# Revit family: Roof-Windows_VELUX_GGLS(2)
name_source: partatom
category: Windows
revit_build: Autodesk Revit 2015 (Build: 20140606_1530(x64)
units: mm (PartAtom-declared; Revit-internal decimal feet)

## types (1)
- GGL Studio - 3x FK06
    AllowedRoofSlope = 15°-90°
    Analytic Construction = <None>
    Angle = 0.00°
    Assembly Code = B3020110
    AssemblyPlace = insitu
    CladdingMaterial = Two layers of aluminium
    CoatingInterior = white paint color NCS 0500-N
    Description = https://bimobject.com
    DistanceBetweenPanels = 588.5 mm  [stored 1.93077 ft]
    Edition number = 1
    FireExit = No
    FireRating = 0
    FlashingMaterial = Two layers of aluminium
    FrameArea = 0.75 m²
    Function = 2 x pivot hung roof window + 1 fixed
    GlassColour = Clear
    GlassLayers = 0
    GlassThickness1 = 0 mm  [stored 0 ft]
    GlassThickness2 = 0 mm  [stored 0 ft]
    GlassThickness3 = 0 mm  [stored 0 ft]
    Glazing = Glass
    GlazingArea = 1.41 m²
    GlazingAreaFraction = 0
    HasDrive = No
    HasExteriorShading = No
    HasInteriorShading = No
    HasSillExternal = Yes
    HasSillInternal = Yes
    Height = 1178 mm  [stored 3.86483 ft]
    Infiltration = 0
    IsExternal = Yes
    IsLaminated = Yes
    IsSolarPowered = No
    IsTempered = Yes
    IsWired = No
    LiningBendFromFrame = 66 mm
    LiningBendFromRoof = 155.3 mm  [stored 0.509514 ft]
    Manufacturer = VELUX A/S
    MaterialExterior = Aluminium. Color NCS 7500-N
    Model = GGLS
    OffsetFromRoof = 135.5 mm
    OpenWindow = No
    OpeningLines = Yes
    Operation = MANUAL
    PanelOffset = -119 mm
    PanelWidth = 641.8 mm
    PerimeterGlazing = 8.79 mm
    PerimeterWindow = 6.03 mm
    Product Guid = 619879da-f779-4aaa-8708-ee59bcbfb10d
    Product data url = https://www.bimobject.com
    ShadingCoefficient = 0
    SolarAbsorption = 0
    SolarHeatGainTransmittance = 0
    SolarReflectance = 0
    SolarTransmittance = 0
    ThermalBridgeGlazing = 0
    ThermalBridgeInstallation = 0
    ThermalTransmittance = 0
    ThermalTransmittanceGlazing = 0
    ThicknessOfRoofMaterial = 40 mm
    URL = http://www.velux.com
    VentilationSlotArea = 0 m²
    VentilationSlotFlow = 0
    VisibleLightReflectance = 0
    VisibleLightTransmittance = 0
    WarrantyYears = 10
    Width = 1837 mm  [stored 6.0269 ft]
    WindowArea = 2.16 m²
    WindowOpeningAngle = 0.00°
    g-value = 0

note: [stored X ft] marks values corroborated as IEEE doubles in the binary element streams (Revit-internal decimal feet)

## geometry (parser evidence)
native form markers: Blend x20, Sweep x7
no freeform markers — native parametric forms only
